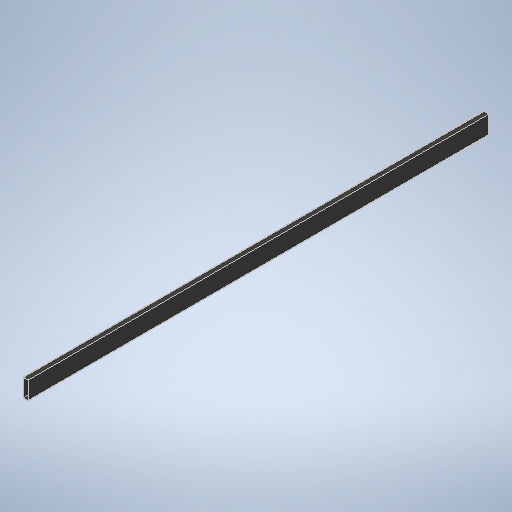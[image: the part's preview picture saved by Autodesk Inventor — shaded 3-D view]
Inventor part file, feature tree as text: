
AUTODESK INVENTOR PART (.ipt)
format: ipt  version: 2025 (Build 290162010, 162A)  size: 252,928 bytes
history: native  units: in
note: dims shown in document units (in); Inventor stores cm internally (conversion verified against a paired STEP export)
features: extrude x1, sketch x1
ambient origin geometry x8: Origin, YZ Plane, XZ Plane, XY Plane, X Axis, Y Axis, Z Axis, Center Point
bodies: Solid1 (feature_tree)
feature tree (2):
  extrude  "Extrusion1"  Depth=1.5in
  sketch  "Sketch1"  dims[d1=5.5in d2=1.5in d3=0.0625in d4=144.0in d5=0.0in]
